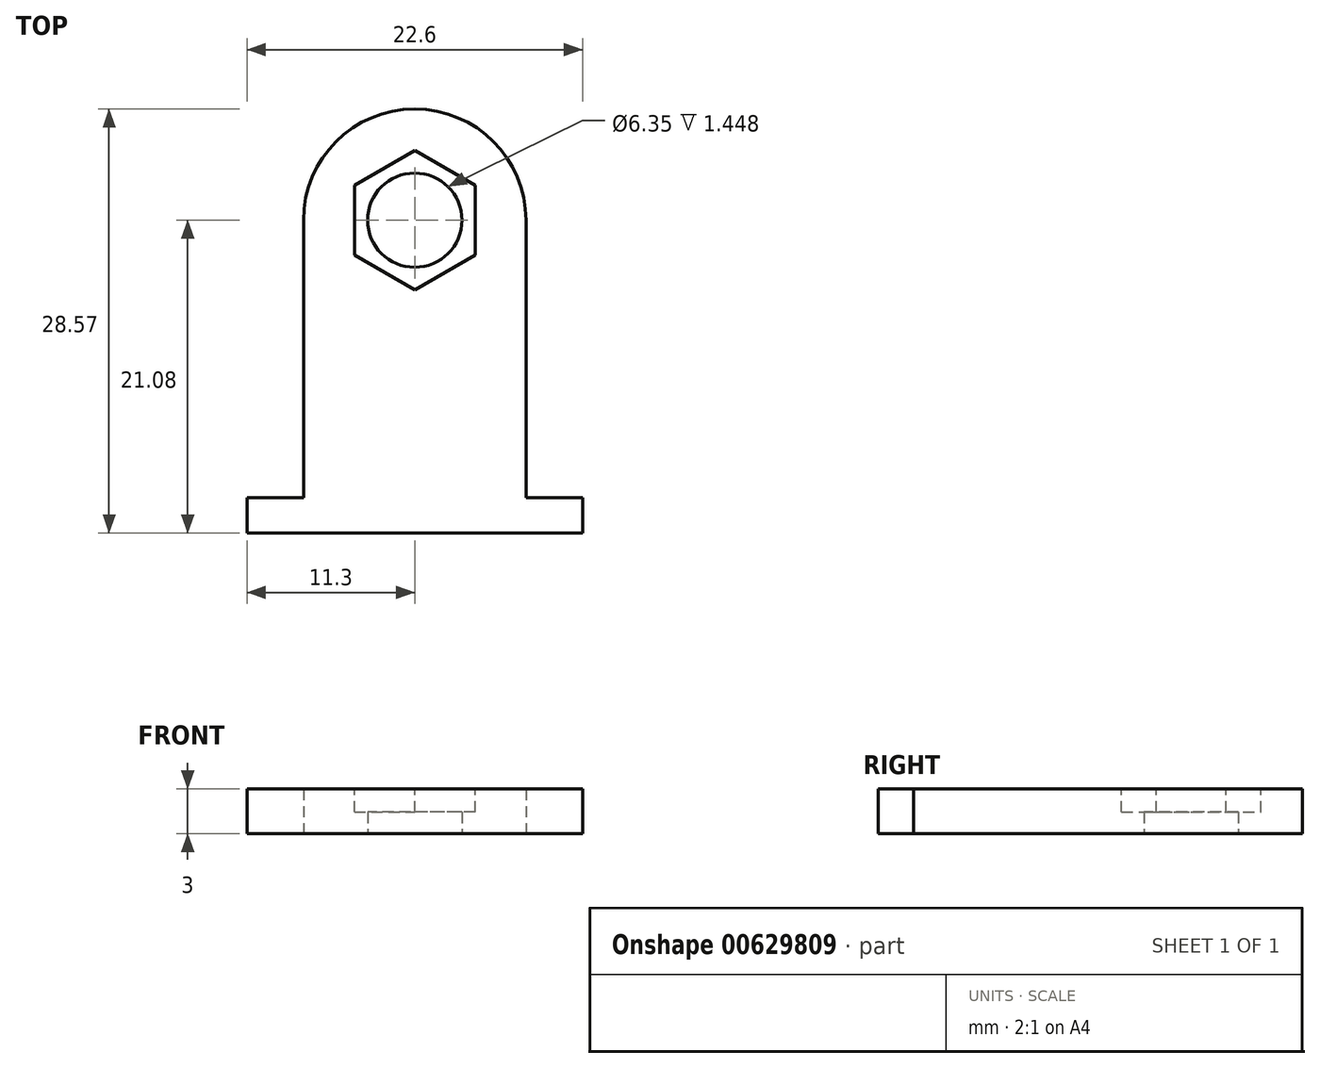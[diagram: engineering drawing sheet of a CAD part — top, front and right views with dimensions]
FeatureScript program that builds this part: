
annotation { "Feature Type Name" : "Feature", "Feature Type Description" : "" }
export const myFeature = defineFeature(function(context is Context, id is Id, definition is map)
    precondition{}
    {
        {
            var Q0;
            Q0=qCreatedBy(makeId("Top.planeOp"),FACE);
            var sketch = newSketch(context, id + "F0", { "sketchPlane" : qUnion([Q0])});
            skLineSegment(sketch, "E0.left", {"start": v(-7.5, 0) * mm, "end": v(-7.5, -18.7) * mm});
            skLineSegment(sketch, "E0.right", {"start": v(7.5, 0) * mm, "end": v(7.5, -18.7) * mm});
            skLineSegment(sketch, "E1.bottom", {"start": v(-11.3, -18.7) * mm, "end": v(-7.5, -18.7) * mm});
            skLineSegment(sketch, "E1.top", {"start": v(-11.3, -21.08) * mm, "end": v(11.3, -21.08) * mm});
            skLineSegment(sketch, "E1.left", {"start": v(-11.3, -18.7) * mm, "end": v(-11.3, -21.08) * mm});
            skLineSegment(sketch, "E1.right", {"start": v(11.3, -18.7) * mm, "end": v(11.3, -21.08) * mm});
            skLineSegment(sketch, "E2.trimOffspring", {"start": v(7.5, -18.7) * mm, "end": v(11.3, -18.7) * mm});
            skArc(sketch, "E3", {"start": v(7.5, 0) * mm, "mid": v(0, 7.5) * mm, "end": v(-7.5, 0) * mm});
            skCircle(sketch, "E4", {"center": v(0, 0) * mm, "radius": 3.18 * mm});
            skLineSegment(sketch, "E5", {"start": v(7.5, 0) * mm, "end": v(-7.5, 0) * mm});
            skSolve(sketch);
        }
        {
            var Q0;
            Q0=qSketchRegion(id+"F0",true);
            extrude(context, id + "F1", {"entities" : qUnion([Q0]), "depth" : 3 * mm, "offsetDistance" : 25.4 * mm});
        }
        {
            var Q0;
            Q0=makeQuery(id+"F1.opExtrude","CAP_FACE",FACE,{"disambiguationData":[OSD([sQuery(id+"F0.wireOp",EDGE,"E0.left"),sQuery(id+"F0.wireOp",EDGE,"E0.right"),sQuery(id+"F0.wireOp",EDGE,"E1.bottom"),sQuery(id+"F0.wireOp",EDGE,"E1.top"),sQuery(id+"F0.wireOp",EDGE,"E1.left"),sQuery(id+"F0.wireOp",EDGE,"E1.right"),sQuery(id+"F0.wireOp",EDGE,"E2.trimOffspring"),sQuery(id+"F0.wireOp",EDGE,"E3"),sQuery(id+"F0.wireOp",EDGE,"E4")])],"isStart":false});
            var sketch = newSketch(context, id + "F2", { "sketchPlane" : qUnion([Q0])});
            skCircle(sketch, "E6.cCircle", {"center": v(0, 0) * mm, "radius": 4.06 * mm, "construction": true});
            skLineSegment(sketch, "E6.0", {"start": v(-4.06, 2.35) * mm, "end": v(0, 4.7) * mm});
            skLineSegment(sketch, "E6.1", {"start": v(0, 4.7) * mm, "end": v(4.06, 2.35) * mm});
            skLineSegment(sketch, "E6.2", {"start": v(4.06, 2.35) * mm, "end": v(4.06, -2.35) * mm});
            skLineSegment(sketch, "E6.3", {"start": v(4.06, -2.35) * mm, "end": v(0, -4.7) * mm});
            skLineSegment(sketch, "E6.4", {"start": v(0, -4.7) * mm, "end": v(-4.06, -2.35) * mm});
            skLineSegment(sketch, "E6.5", {"start": v(-4.06, -2.35) * mm, "end": v(-4.06, 2.35) * mm});
            skPoint(sketch, "E6.0.midPoint", {"position": v(-2.03, 3.52) * mm});
            skSolve(sketch);
        }
        {
            var Q0;
            Q0 = qSketchRegion(id + "F2", true);
            extrude(context, id + "F3", {"entities" : qUnion([Q0]), "operationType" : NewBodyOperationType.REMOVE, "oppositeDirection" : true, "depth" : 1.55 * mm, "offsetDistance" : 25.4 * mm});
        }
    });
